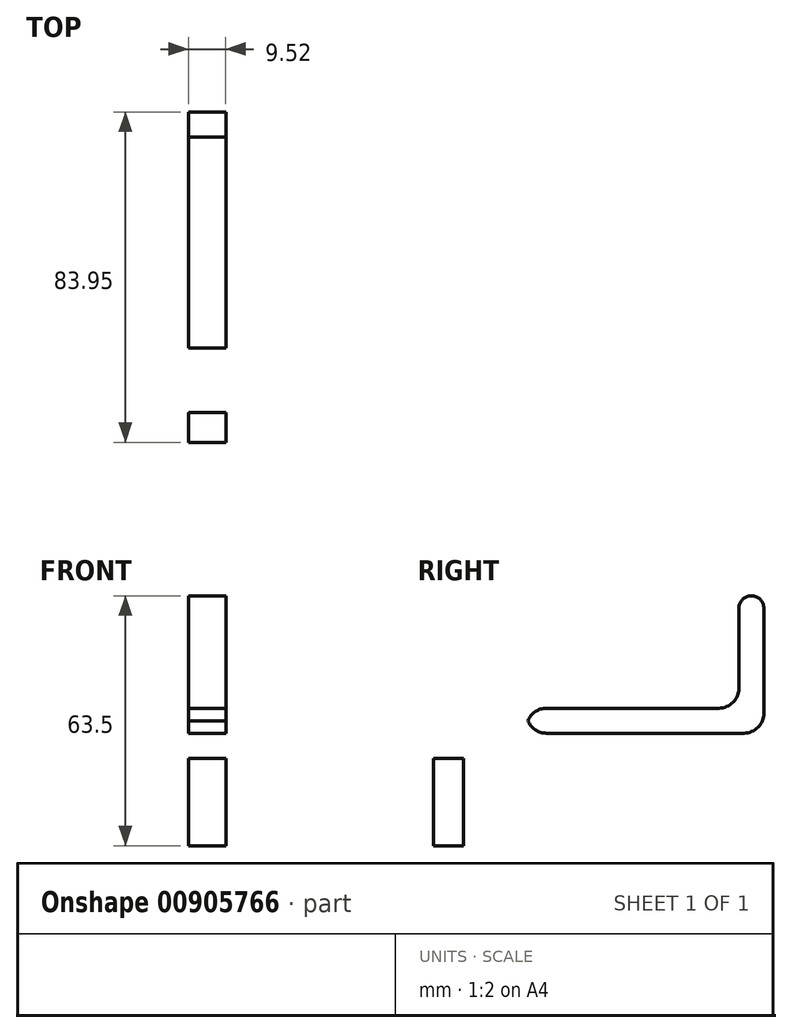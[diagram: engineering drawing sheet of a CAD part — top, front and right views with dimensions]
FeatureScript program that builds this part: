
annotation { "Feature Type Name" : "Feature", "Feature Type Description" : "" }
export const myFeature = defineFeature(function(context is Context, id is Id, definition is map)
    precondition{}
    {
        {
            var Q0;
            Q0=qCreatedBy(makeId("Right.planeOp"),FACE);
            var sketch = newSketch(context, id + "F0", { "sketchPlane" : qUnion([Q0])});
            skArc(sketch, "E0", {"start": v(-21.93, 3.94) * mm, "mid": v(-17.74, 8.13) * mm, "end": v(-13.55, 3.94) * mm});
            skLineSegment(sketch, "E1", {"start": v(-13.55, 3.94) * mm, "end": v(-13.55, -2.41) * mm});
            skLineSegment(sketch, "E2", {"start": v(-29.55, -8.76) * mm, "end": v(-29.55, -30.99) * mm});
            skLineSegment(sketch, "E3", {"start": v(-21.93, 3.94) * mm, "end": v(-21.93, 0.76) * mm});
            skLineSegment(sketch, "E4.0", {"start": v(-29.55, 3.94) * mm, "end": v(-29.55, 0.76) * mm});
            skArc(sketch, "E4.1", {"start": v(-29.55, 3.94) * mm, "mid": v(-17.74, 15.75) * mm, "end": v(-5.93, 3.94) * mm});
            skLineSegment(sketch, "E4.2", {"start": v(-5.93, 3.94) * mm, "end": v(-5.93, -2.41) * mm});
            skLineSegment(sketch, "E5.1", {"start": v(-21.93, -8.76) * mm, "end": v(-21.93, -30.99) * mm});
            skLineSegment(sketch, "E6", {"start": v(-29.55, -30.99) * mm, "end": v(-21.93, -30.99) * mm});
            skLineSegment(sketch, "E7", {"start": v(-29.55, 0.76) * mm, "end": v(-21.93, 0.76) * mm});
            skArc(sketch, "E8", {"start": v(-13.55, -2.41) * mm, "mid": v(-16.16, -7.67) * mm, "end": v(-21.93, -8.76) * mm});
            skLineSegment(sketch, "E9", {"start": v(-29.55, -8.76) * mm, "end": v(-21.93, -8.76) * mm});
            skArc(sketch, "E10.0", {"start": v(-5.93, -2.41) * mm, "mid": v(-10.75, -13.08) * mm, "end": v(-21.93, -16.52) * mm});
            skLineSegment(sketch, "E11.bottom", {"start": v(-5.93, 3.94) * mm, "end": v(54.4, 3.94) * mm});
            skLineSegment(sketch, "E11.top", {"start": v(-5.93, -2.41) * mm, "end": v(54.4, -2.41) * mm});
            skLineSegment(sketch, "E11.right", {"start": v(54.4, 3.94) * mm, "end": v(54.4, -2.41) * mm});
            skPoint(sketch, "E12", {"position": v(28.42, 0.76) * mm});
            skLineSegment(sketch, "E13.bottom", {"start": v(54.4, 3.94) * mm, "end": v(48.05, 3.94) * mm});
            skLineSegment(sketch, "E13.top", {"start": v(54.4, 29.34) * mm, "end": v(48.05, 29.34) * mm});
            skLineSegment(sketch, "E13.left", {"start": v(54.4, 3.94) * mm, "end": v(54.4, 29.34) * mm});
            skLineSegment(sketch, "E13.right", {"start": v(48.05, 3.94) * mm, "end": v(48.05, 29.34) * mm});
            skArc(sketch, "E14", {"start": v(54.4, 29.34) * mm, "mid": v(51.22, 32.51) * mm, "end": v(48.05, 29.34) * mm});
            skSolve(sketch);
        }
        {
            var Q0;
            Q0=makeQuery(id+"F0.imprint","IMPRINT",FACE,{"disambiguationData":[TD([[makeQuery(id+"F0.imprint","IMPRINT",EDGE,{"derivedFrom":sQuery(id+"F0.wireOp",EDGE,"E0")}),1.0]])]});
            var Q1;
            Q1=makeQuery(id+"F0.imprint","IMPRINT",FACE,{"disambiguationData":[TD([[makeQuery(id+"F0.imprint","IMPRINT",EDGE,{"derivedFrom":sQuery(id+"F0.wireOp",EDGE,"E2")}),1.0]])]});
            var Q2;
            {var subQ3=sQuery(id+"F0.wireOp",EDGE,"E4.2");Q2=makeQuery(id+"F0.imprint","IMPRINT",FACE,{"disambiguationData":[TD([[makeQuery(id+"F0.imprint","IMPRINT",EDGE,{"derivedFrom":subQ3}),1.0]])]});}
            var Q3;
            Q3=makeQuery(id+"F0.imprint","IMPRINT",FACE,{"disambiguationData":[TD([[makeQuery(id+"F0.imprint","IMPRINT",EDGE,{"derivedFrom":sQuery(id+"F0.wireOp",EDGE,"E13.top")}),1.0]])]});
            var Q4;
            Q4=makeQuery(id+"F0.imprint","IMPRINT",FACE,{"disambiguationData":[TD([[makeQuery(id+"F0.imprint","IMPRINT",EDGE,{"derivedFrom":sQuery(id+"F0.wireOp",EDGE,"E13.top")}),-1.0]])]});
            extrude(context, id + "F1", {"entities" : qUnion([Q0, Q1, Q2, Q3, Q4]), "depth" : 9.52 * mm, "offsetDistance" : 25.4 * mm, "symmetric" : true});
        }
        {
            var Q0;
            Q0=makeQuery(id+"F1.opExtrude","SWEPT_EDGE",EDGE,{"disambiguationData":[OSD([sQuery(id+"F0.wireOp",EDGE,"E11.top"),sQuery(id+"F0.wireOp",EDGE,"E11.right")])]});
            var Q1;
            Q1=makeQuery(id+"F1.opExtrude","SWEPT_EDGE",EDGE,{"disambiguationData":[OSD([sQuery(id+"F0.wireOp",EDGE,"E11.bottom"),sQuery(id+"F0.wireOp",EDGE,"E13.right")])]});
            var Q2;
            Q2=makeQuery(id+"F1.opExtrude","SWEPT_EDGE",EDGE,{"disambiguationData":[OSD([sQuery(id+"F0.wireOp",EDGE,"E4.1"),sQuery(id+"F0.wireOp",EDGE,"E4.2"),sQuery(id+"F0.wireOp",EDGE,"E11.bottom")])]});
            var Q3;
            Q3=makeQuery(id+"F1.opExtrude","SWEPT_EDGE",EDGE,{"disambiguationData":[OSD([sQuery(id+"F0.wireOp",EDGE,"E4.2"),sQuery(id+"F0.wireOp",EDGE,"E10.0"),sQuery(id+"F0.wireOp",EDGE,"E11.top")])]});
            fillet(context, id + "F2", {"entities" : qUnion([Q0, Q1, Q2, Q3]), "radius" : 5.08 * mm, "tangentPropagation" : true, "allowEdgeOverflow" : false});
        }
    });
